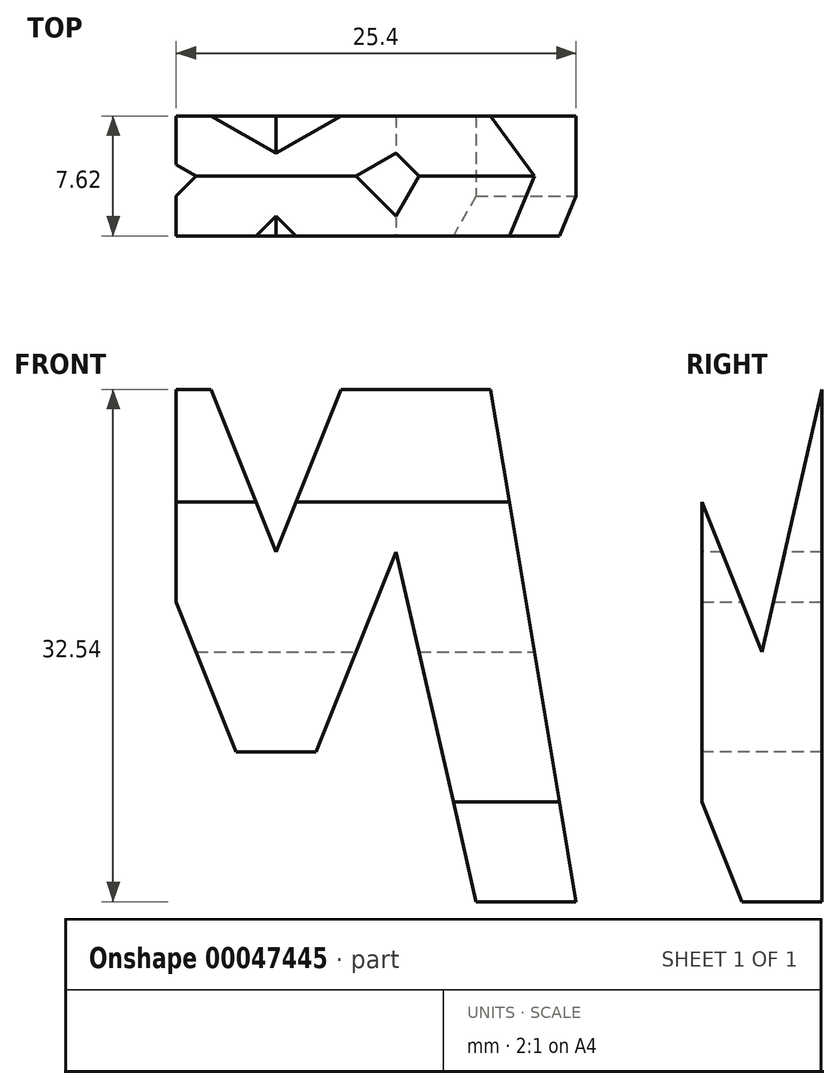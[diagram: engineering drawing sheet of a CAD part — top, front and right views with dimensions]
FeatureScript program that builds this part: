
annotation { "Feature Type Name" : "Feature", "Feature Type Description" : "" }
export const myFeature = defineFeature(function(context is Context, id is Id, definition is map)
    precondition{}
    {
        {
            var Q0;
            Q0=qCreatedBy(makeId("Front.planeOp"),FACE);
            var sketch = newSketch(context, id + "F0", { "sketchPlane" : qUnion([Q0])});
            skLineSegment(sketch, "E0.bottom", {"start": v(0, 0) * mm, "end": v(38.1, 0) * mm});
            skLineSegment(sketch, "E0.top", {"start": v(0, 38.1) * mm, "end": v(38.1, 38.1) * mm});
            skLineSegment(sketch, "E0.left", {"start": v(0, 0) * mm, "end": v(0, 38.1) * mm});
            skLineSegment(sketch, "E0.right", {"start": v(38.1, 0) * mm, "end": v(38.1, 38.1) * mm});
            skSolve(sketch);
        }
        {
            var Q0;
            Q0 = qSketchRegion(id + "F0", true);
            extrude(context, id + "F1", {"entities" : qUnion([Q0]), "depth" : 38.1 * mm});
        }
        {
            var Q0;
            Q0=qCreatedBy(makeId("Front.planeOp"),FACE);
            cPlane(context, id + "F2", {"entities" : qUnion([Q0]), "cplaneType" : CPlaneType.OFFSET, "offset" : 38.1 * mm, "width" : 152.4 * mm, "height" : 152.4 * mm});
        }
        {
            var Q0;
            Q0=qCreatedBy(makeId("Right.planeOp"),FACE);
            cPlane(context, id + "F3", {"entities" : qUnion([Q0]), "cplaneType" : CPlaneType.OFFSET, "offset" : 38.1 * mm, "width" : 152.4 * mm, "height" : 152.4 * mm});
        }
        {
            var Q0;
            Q0=qCreatedBy(makeId("Top.planeOp"),FACE);
            cPlane(context, id + "F4", {"entities" : qUnion([Q0]), "cplaneType" : CPlaneType.OFFSET, "offset" : 38.1 * mm, "width" : 152.4 * mm, "height" : 152.4 * mm});
        }
        {
            var Q0;
            Q0=qCreatedBy(id+"F3.planeOp",FACE);
            var sketch = newSketch(context, id + "F5", { "sketchPlane" : qUnion([Q0])});
            skLineSegment(sketch, "E1.bottom", {"start": v(0, 0) * mm, "end": v(-38.1, 0) * mm});
            skLineSegment(sketch, "E1.top", {"start": v(0, 38.1) * mm, "end": v(-38.1, 38.1) * mm});
            skLineSegment(sketch, "E1.left", {"start": v(0, 0) * mm, "end": v(0, 38.1) * mm});
            skLineSegment(sketch, "E1.right", {"start": v(-38.1, 0) * mm, "end": v(-38.1, 38.1) * mm});
            skLineSegment(sketch, "E2", {"start": v(-38.1, 38.1) * mm, "end": v(-31.75, 0) * mm});
            skLineSegment(sketch, "E3", {"start": v(-31.75, 0) * mm, "end": v(-25.4, 0) * mm});
            skLineSegment(sketch, "E4", {"start": v(-25.4, 0) * mm, "end": v(-19.05, 15.88) * mm});
            skLineSegment(sketch, "E5", {"start": v(-19.05, 15.88) * mm, "end": v(-12.7, 0) * mm});
            skLineSegment(sketch, "E6", {"start": v(-12.7, 0) * mm, "end": v(-6.35, 0) * mm});
            skLineSegment(sketch, "E7", {"start": v(-6.35, 0) * mm, "end": v(0, 38.1) * mm});
            skLineSegment(sketch, "E8", {"start": v(-6.35, 38.1) * mm, "end": v(-11.43, 15.87) * mm});
            skLineSegment(sketch, "E9", {"start": v(-11.43, 15.87) * mm, "end": v(-16.51, 28.58) * mm});
            skLineSegment(sketch, "E10", {"start": v(-16.51, 28.58) * mm, "end": v(-21.6, 28.58) * mm});
            skLineSegment(sketch, "E11", {"start": v(-21.6, 28.58) * mm, "end": v(-26.67, 15.87) * mm});
            skLineSegment(sketch, "E12", {"start": v(-26.67, 15.87) * mm, "end": v(-31.75, 38.1) * mm});
            skLineSegment(sketch, "E13", {"start": v(-31.75, 38.1) * mm, "end": v(-38.1, 38.1) * mm});
            skSolve(sketch);
        }
        {
            var Q0;
            {var subQ0=sQuery(id+"F5.wireOp",EDGE,"E8");Q0=makeQuery(id+"F5.imprint","IMPRINT",FACE,{"disambiguationData":[TD([[makeQuery(id+"F5.imprint","IMPRINT",EDGE,{"derivedFrom":subQ0}),-1.0]])]});}
            var Q1;
            {var subQ0=sQuery(id+"F5.wireOp",EDGE,"E1.right");Q1=makeQuery(id+"F5.imprint","IMPRINT",FACE,{"disambiguationData":[TD([[makeQuery(id+"F5.imprint","IMPRINT",EDGE,{"derivedFrom":subQ0}),-1.0]])]});}
            var Q2;
            {var subQ0=sQuery(id+"F5.wireOp",EDGE,"E4");Q2=makeQuery(id+"F5.imprint","IMPRINT",FACE,{"disambiguationData":[TD([[makeQuery(id+"F5.imprint","IMPRINT",EDGE,{"derivedFrom":subQ0}),-1.0]])]});}
            var Q3;
            {var subQ0=sQuery(id+"F5.wireOp",EDGE,"E1.left");Q3=makeQuery(id+"F5.imprint","IMPRINT",FACE,{"disambiguationData":[TD([[makeQuery(id+"F5.imprint","IMPRINT",EDGE,{"derivedFrom":subQ0}),1.0]])]});}
            extrude(context, id + "F6", {"entities" : qUnion([Q0, Q1, Q2, Q3]), "operationType" : NewBodyOperationType.REMOVE, "oppositeDirection" : true, "depth" : 38.1 * mm});
        }
        {
            var Q0;
            Q0=qCreatedBy(id+"F2.planeOp",FACE);
            var sketch = newSketch(context, id + "F7", { "sketchPlane" : qUnion([Q0])});
            skLineSegment(sketch, "E14.bottom", {"start": v(0, 0) * mm, "end": v(38.1, 0) * mm});
            skLineSegment(sketch, "E14.top", {"start": v(0, 38.1) * mm, "end": v(38.1, 38.1) * mm});
            skLineSegment(sketch, "E14.left", {"start": v(0, 0) * mm, "end": v(0, 38.1) * mm});
            skLineSegment(sketch, "E14.right", {"start": v(38.1, 0) * mm, "end": v(38.1, 38.1) * mm});
            skLineSegment(sketch, "E15", {"start": v(0, 0) * mm, "end": v(6.35, 38.1) * mm});
            skLineSegment(sketch, "E16", {"start": v(6.35, 38.1) * mm, "end": v(12.7, 38.1) * mm});
            skLineSegment(sketch, "E17", {"start": v(12.7, 38.1) * mm, "end": v(19.05, 22.22) * mm});
            skLineSegment(sketch, "E18", {"start": v(19.05, 22.22) * mm, "end": v(25.4, 38.1) * mm});
            skLineSegment(sketch, "E19", {"start": v(25.4, 38.1) * mm, "end": v(31.75, 38.1) * mm});
            skLineSegment(sketch, "E20", {"start": v(31.75, 38.1) * mm, "end": v(38.1, 0) * mm});
            skLineSegment(sketch, "E21", {"start": v(31.75, 0) * mm, "end": v(26.67, 22.23) * mm});
            skLineSegment(sketch, "E22", {"start": v(26.67, 22.23) * mm, "end": v(21.59, 9.52) * mm});
            skLineSegment(sketch, "E23", {"start": v(21.6, 9.52) * mm, "end": v(16.51, 9.52) * mm});
            skLineSegment(sketch, "E24", {"start": v(16.51, 9.52) * mm, "end": v(11.43, 22.23) * mm});
            skLineSegment(sketch, "E25", {"start": v(11.43, 22.23) * mm, "end": v(6.35, 0) * mm});
            skLineSegment(sketch, "E26", {"start": v(6.35, 0) * mm, "end": v(0, 0) * mm});
            skSolve(sketch);
        }
        {
            var Q0;
            {var subQ0=sQuery(id+"F7.wireOp",EDGE,"E14.left");Q0=makeQuery(id+"F7.imprint","IMPRINT",FACE,{"disambiguationData":[TD([[makeQuery(id+"F7.imprint","IMPRINT",EDGE,{"derivedFrom":subQ0}),-1.0]])]});}
            var Q1;
            {var subQ0=sQuery(id+"F7.wireOp",EDGE,"E17");Q1=makeQuery(id+"F7.imprint","IMPRINT",FACE,{"disambiguationData":[TD([[makeQuery(id+"F7.imprint","IMPRINT",EDGE,{"derivedFrom":subQ0}),1.0]])]});}
            var Q2;
            {var subQ0=sQuery(id+"F7.wireOp",EDGE,"E14.right");Q2=makeQuery(id+"F7.imprint","IMPRINT",FACE,{"disambiguationData":[TD([[makeQuery(id+"F7.imprint","IMPRINT",EDGE,{"derivedFrom":subQ0}),1.0]])]});}
            var Q3;
            {var subQ2=sQuery(id+"F7.wireOp",EDGE,"E21");Q3=makeQuery(id+"F7.imprint","IMPRINT",FACE,{"disambiguationData":[TD([[makeQuery(id+"F7.imprint","IMPRINT",EDGE,{"derivedFrom":subQ2}),1.0]])]});}
            extrude(context, id + "F8", {"entities" : qUnion([Q0, Q1, Q2, Q3]), "operationType" : NewBodyOperationType.REMOVE, "oppositeDirection" : true, "depth" : 38.1 * mm});
        }
        {
            var Q0;
            Q0=qCreatedBy(id+"F4.planeOp",FACE);
            var sketch = newSketch(context, id + "F9", { "sketchPlane" : qUnion([Q0])});
            skLineSegment(sketch, "E27.bottom", {"start": v(0, 0) * mm, "end": v(38.1, 0) * mm});
            skLineSegment(sketch, "E27.top", {"start": v(0, -38.1) * mm, "end": v(38.1, -38.1) * mm});
            skLineSegment(sketch, "E27.left", {"start": v(0, 0) * mm, "end": v(0, -38.1) * mm});
            skLineSegment(sketch, "E27.right", {"start": v(38.1, 0) * mm, "end": v(38.1, -38.1) * mm});
            skLineSegment(sketch, "E28", {"start": v(38.1, 0) * mm, "end": v(0, 0) * mm});
            skLineSegment(sketch, "E29", {"start": v(0, -22.86) * mm, "end": v(25.4, -22.86) * mm});
            skLineSegment(sketch, "E30", {"start": v(25.4, -22.86) * mm, "end": v(25.4, -30.48) * mm});
            skLineSegment(sketch, "E31", {"start": v(25.4, -30.48) * mm, "end": v(0, -30.48) * mm});
            skLineSegment(sketch, "E32", {"start": v(0, -30.48) * mm, "end": v(0, -38.1) * mm});
            skLineSegment(sketch, "E33", {"start": v(38.1, -38.1) * mm, "end": v(38.1, -15.24) * mm});
            skLineSegment(sketch, "E34", {"start": v(38.1, -15.24) * mm, "end": v(12.7, -15.24) * mm});
            skLineSegment(sketch, "E35", {"start": v(12.7, -15.24) * mm, "end": v(12.7, -7.62) * mm});
            skLineSegment(sketch, "E36", {"start": v(12.7, -7.62) * mm, "end": v(38.1, -7.62) * mm});
            skLineSegment(sketch, "E37", {"start": v(38.1, -7.62) * mm, "end": v(38.1, 0) * mm});
            skSolve(sketch);
        }
        {
            var Q0;
            Q0=makeQuery(id+"F9.imprint","IMPRINT",FACE,{"disambiguationData":[TD([[makeQuery(id+"F9.imprint","IMPRINT",EDGE,{"derivedFrom":sQuery(id+"F9.wireOp",EDGE,"E27.right")}),-1.0]])]});
            var Q1;
            {var subQ2=sQuery(id+"F9.wireOp",EDGE,"E29");Q1=makeQuery(id+"F9.imprint","IMPRINT",FACE,{"disambiguationData":[TD([[makeQuery(id+"F9.imprint","IMPRINT",EDGE,{"derivedFrom":subQ2}),-1.0]])]});}
            extrude(context, id + "F10", {"entities" : qUnion([Q0, Q1]), "operationType" : NewBodyOperationType.REMOVE, "oppositeDirection" : true, "depth" : 38.1 * mm});
        }
    });
